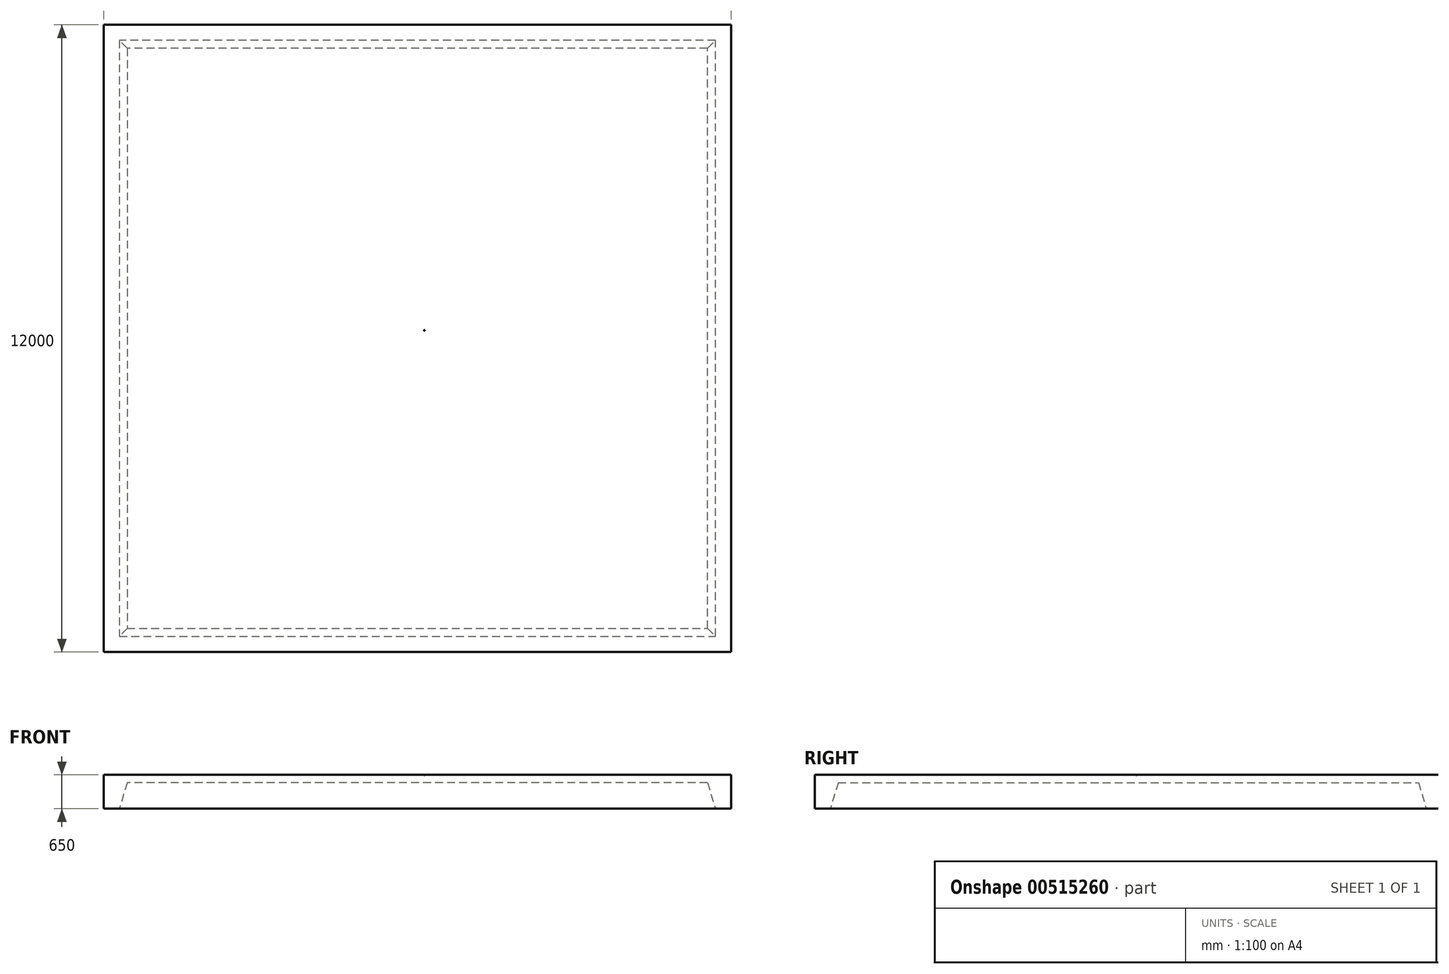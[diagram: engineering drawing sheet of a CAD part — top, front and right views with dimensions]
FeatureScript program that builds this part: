
annotation { "Feature Type Name" : "Feature", "Feature Type Description" : "" }
export const myFeature = defineFeature(function(context is Context, id is Id, definition is map)
    precondition{}
    {
        {
            var Q0;
            Q0=qCreatedBy(makeId("Top.planeOp"),FACE);
            var sketch = newSketch(context, id + "F0", { "sketchPlane" : qUnion([Q0])});
            skLineSegment(sketch, "E0.bottom", {"start": v(-6000, 6000) * mm, "end": v(6000, 6000) * mm});
            skLineSegment(sketch, "E0.top", {"start": v(-6000, -6000) * mm, "end": v(6000, -6000) * mm});
            skLineSegment(sketch, "E0.left", {"start": v(-6000, 6000) * mm, "end": v(-6000, -6000) * mm});
            skLineSegment(sketch, "E0.right", {"start": v(6000, 6000) * mm, "end": v(6000, -6000) * mm});
            skSolve(sketch);
        }
        {
            var Q0;
            Q0=qCreatedBy(makeId("Right.planeOp"),FACE);
            var sketch = newSketch(context, id + "F1", { "sketchPlane" : qUnion([Q0])});
            skLineSegment(sketch, "E1", {"start": v(-6000, 0) * mm, "end": v(-6000, -500) * mm});
            skLineSegment(sketch, "E2", {"start": v(-6000, -500) * mm, "end": v(-5700, -500) * mm});
            skLineSegment(sketch, "E3", {"start": v(-5700, -500) * mm, "end": v(-5550, 0) * mm});
            skLineSegment(sketch, "E4", {"start": v(-5550, 0) * mm, "end": v(-6000, 0) * mm});
            skSolve(sketch);
        }
        {
            var Q0;
            Q0=makeQuery(id+"F1.imprint","IMPRINT",FACE,{"disambiguationData":[TD([[makeQuery(id+"F1.imprint","IMPRINT",EDGE,{"derivedFrom":sQuery(id+"F1.wireOp",EDGE,"E1")}),1.0]])]});
            var Q1;
            Q1=sQuery(id+"F0.wireOp",EDGE,"E0.top");
            var Q2;
            Q2=sQuery(id+"F0.wireOp",EDGE,"E0.left");
            var Q3;
            Q3=sQuery(id+"F0.wireOp",EDGE,"E0.bottom");
            var Q4;
            Q4=sQuery(id+"F0.wireOp",EDGE,"E0.right");
            sweep(context, id + "F2", {"profiles" : qUnion([Q0]), "path" : qUnion([Q1, Q2, Q3, Q4])});
        }
        {
            var Q0;
            Q0 = qSketchRegion(id + "F0", true);
            extrude(context, id + "F3", {"entities" : qUnion([Q0]), "operationType" : NewBodyOperationType.ADD, "depth" : 150 * mm, "offsetDistance" : 25 * mm});
        }
        {
            var Q0;
            Q0=makeQuery(id+"F3.opExtrude","CAP_FACE",FACE,{"disambiguationData":[OSD([sQuery(id+"F0.wireOp",EDGE,"E0.bottom"),sQuery(id+"F0.wireOp",EDGE,"E0.top"),sQuery(id+"F0.wireOp",EDGE,"E0.left"),sQuery(id+"F0.wireOp",EDGE,"E0.right")])],"isStart":false});
            var sketch = newSketch(context, id + "F4", { "sketchPlane" : qUnion([Q0])});
            skCircle(sketch, "E5", {"center": v(132.64, 152.2) * mm, "radius": 1201.04 * mm});
            skSolve(sketch);
        }
        {
            var Q0;
            Q0=sQuery(id+"F4.wireOp",VERTEX,"E5.center");
            var Q1;
            Q1=makeQuery(id+"F2.opSweep","SWEPT_BODY",BODY,{"disambiguationData":[OSD([sQuery(id+"F0.wireOp",EDGE,"E0.left"),sQuery(id+"F1.wireOp",EDGE,"E1"),sQuery(id+"F1.wireOp",EDGE,"E2"),sQuery(id+"F1.wireOp",EDGE,"E3"),sQuery(id+"F1.wireOp",EDGE,"E4")])]});
            hole(context, id + "F5", {"style" : HoleStyle.SIMPLE, "endStyle" : HoleEndStyle.BLIND, "standardTappedOrClearance" : lookupTablePath({ "standard" : "ANSI", "fit" : "Close", "size" : "1/2", "type" : "Clearance" }), "standardBlindInLast" : lookupTablePath({ "fit" : "Close", "standard" : "ANSI", "size" : "1/2", "type" : "Clearance" }), "holeDiameter" : 13.1 * mm, "holeDepth" : 20 * mm, "isTappedThrough" : true, "tappedDepth" : 12 * mm, "tapClearance" : 3, "startFromSketch" : true, "locations" : qUnion([Q0]), "scope" : qUnion([Q1])});
        }
    });
